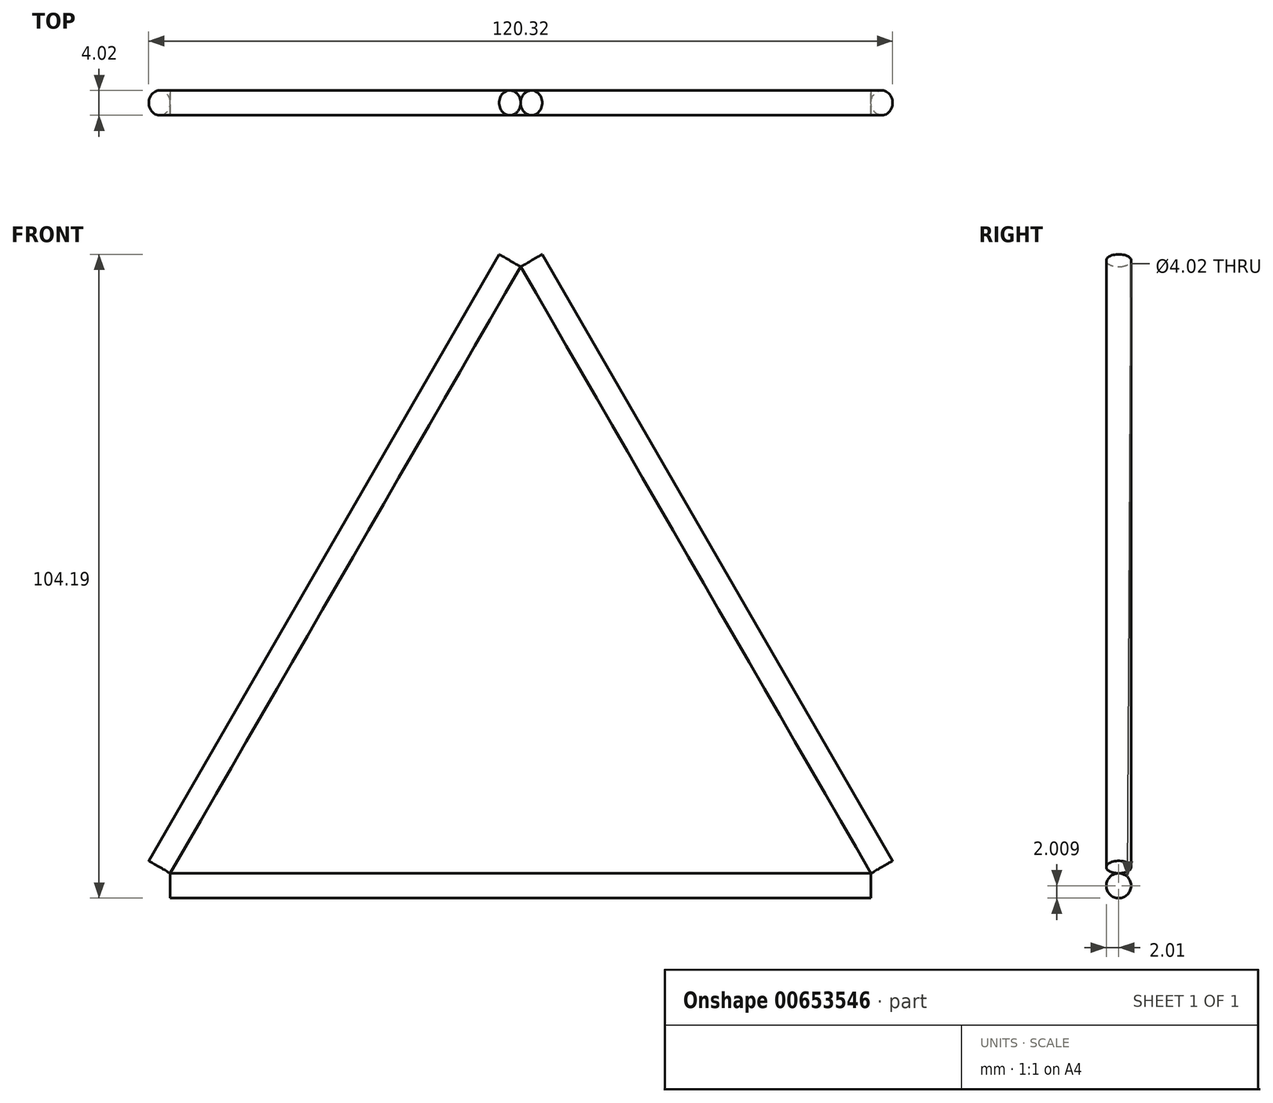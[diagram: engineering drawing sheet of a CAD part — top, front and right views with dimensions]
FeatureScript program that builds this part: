
annotation { "Feature Type Name" : "Feature", "Feature Type Description" : "" }
export const myFeature = defineFeature(function(context is Context, id is Id, definition is map)
    precondition{}
    {
        {
            var Q0;
            Q0=qCreatedBy(makeId("Front.planeOp"),FACE);
            var sketch = newSketch(context, id + "F0", { "sketchPlane" : qUnion([Q0])});
            skCircle(sketch, "E0.cCircle", {"center": v(0, 0) * mm, "radius": 32.72 * mm, "construction": true});
            skLineSegment(sketch, "E0.0", {"start": v(56.67, -32.72) * mm, "end": v(-56.67, -32.72) * mm});
            skLineSegment(sketch, "E0.1", {"start": v(-56.67, -32.72) * mm, "end": v(0, 65.44) * mm});
            skLineSegment(sketch, "E0.2", {"start": v(0, 65.44) * mm, "end": v(56.67, -32.72) * mm});
            skPoint(sketch, "E0.0.midPoint", {"position": v(0, -32.72) * mm});
            skCircle(sketch, "E1.cCircle", {"center": v(0, 0) * mm, "radius": 34.73 * mm, "construction": true});
            skLineSegment(sketch, "E1.0", {"start": v(0, 69.46) * mm, "end": v(60.16, -34.73) * mm});
            skLineSegment(sketch, "E1.1", {"start": v(60.16, -34.73) * mm, "end": v(-60.16, -34.73) * mm});
            skLineSegment(sketch, "E1.2", {"start": v(-60.16, -34.73) * mm, "end": v(0, 69.46) * mm});
            skPoint(sketch, "E1.0.midPoint", {"position": v(30.08, 17.37) * mm});
            skSolve(sketch);
        }
        {
            var Q0;
            Q0=sQuery(id+"F0.wireOp",EDGE,"E0.2");
            var Q1;
            Q1=sQuery(id+"F0.wireOp",EDGE,"E1.0");
            revolve(context, id + "F1", {"bodyType" : ToolBodyType.SURFACE, "surfaceEntities" : qUnion([Q0]), "axis" : qUnion([Q1]), "revolveType" : RevolveType.FULL});
        }
        {
            var Q0;
            Q0=sQuery(id+"F0.wireOp",EDGE,"E0.1");
            var Q1;
            Q1=sQuery(id+"F0.wireOp",EDGE,"E1.2");
            revolve(context, id + "F2", {"bodyType" : ToolBodyType.SURFACE, "surfaceEntities" : qUnion([Q0]), "axis" : qUnion([Q1]), "revolveType" : RevolveType.FULL});
        }
        {
            var Q0;
            Q0=sQuery(id+"F0.wireOp",EDGE,"E0.0");
            var Q1;
            Q1=sQuery(id+"F0.wireOp",EDGE,"E1.1");
            revolve(context, id + "F3", {"bodyType" : ToolBodyType.SURFACE, "surfaceEntities" : qUnion([Q0]), "axis" : qUnion([Q1]), "revolveType" : RevolveType.FULL});
        }
    });
